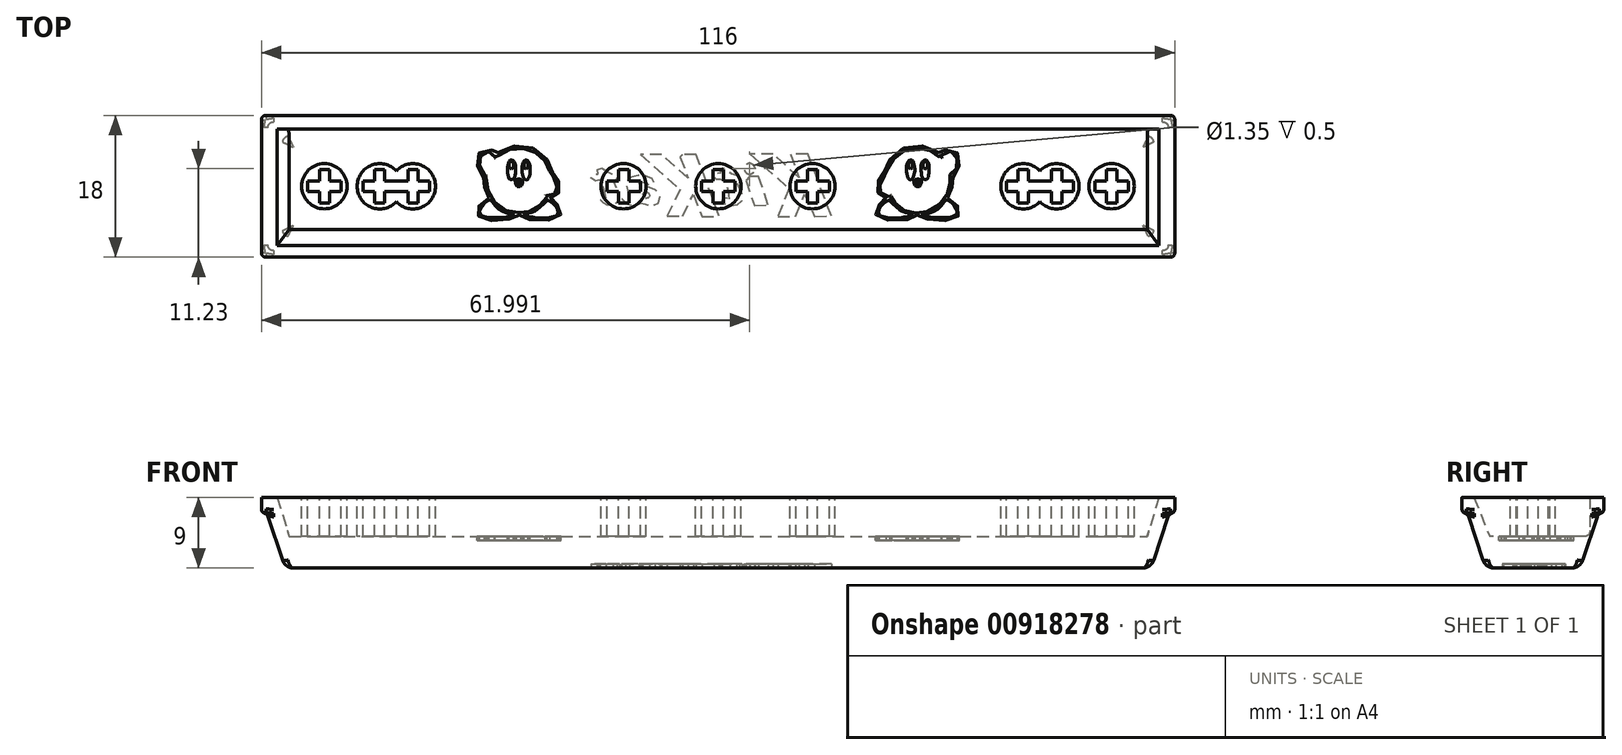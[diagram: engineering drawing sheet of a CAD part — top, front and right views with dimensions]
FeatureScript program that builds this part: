
annotation { "Feature Type Name" : "Feature", "Feature Type Description" : "" }
export const myFeature = defineFeature(function(context is Context, id is Id, definition is map)
    precondition{}
    {
        {
            var Q0;
            Q0=qCreatedBy(makeId("Top.planeOp"),FACE);
            var sketch = newSketch(context, id + "F0", { "sketchPlane" : qUnion([Q0])});
            skLineSegment(sketch, "E0", {"start": v(0, 0) * mm, "end": v(116, 0) * mm});
            skLineSegment(sketch, "E1", {"start": v(116, 0) * mm, "end": v(116, 18) * mm});
            skLineSegment(sketch, "E2", {"start": v(116, 18) * mm, "end": v(0, 18) * mm});
            skLineSegment(sketch, "E3", {"start": v(0, 18) * mm, "end": v(0, 0) * mm});
            skCircle(sketch, "E4", {"center": v(58.02, 9) * mm, "radius": 2.87 * mm});
            skLineSegment(sketch, "E5", {"start": v(60.13, 8.33) * mm, "end": v(58.65, 8.33) * mm});
            skLineSegment(sketch, "E6", {"start": v(55.88, 9.68) * mm, "end": v(57.35, 9.68) * mm});
            skLineSegment(sketch, "E7", {"start": v(57.35, 11.13) * mm, "end": v(57.35, 9.68) * mm});
            skLineSegment(sketch, "E8", {"start": v(58.65, 11.13) * mm, "end": v(58.65, 9.68) * mm});
            skLineSegment(sketch, "E9.trimOffspring", {"start": v(57.35, 8.33) * mm, "end": v(57.35, 6.88) * mm});
            skLineSegment(sketch, "E10.trimOffspring", {"start": v(58.65, 8.33) * mm, "end": v(58.65, 6.88) * mm});
            skLineSegment(sketch, "E11.trimOffspring", {"start": v(58.65, 9.68) * mm, "end": v(60.13, 9.68) * mm});
            skLineSegment(sketch, "E12.trimOffspring", {"start": v(57.35, 8.33) * mm, "end": v(55.88, 8.33) * mm});
            skLineSegment(sketch, "E13", {"start": v(55.88, 9.68) * mm, "end": v(55.88, 8.33) * mm});
            skLineSegment(sketch, "E14", {"start": v(57.35, 11.13) * mm, "end": v(58.65, 11.13) * mm});
            skLineSegment(sketch, "E15", {"start": v(60.13, 9.68) * mm, "end": v(60.13, 8.33) * mm});
            skLineSegment(sketch, "E16", {"start": v(57.35, 6.88) * mm, "end": v(58.65, 6.88) * mm});
            skLineSegment(sketch, "E17.MirrorCS", {"start": v(10.12, 9.68) * mm, "end": v(10.12, 8.33) * mm});
            skLineSegment(sketch, "E18.MirrorCS", {"start": v(7.35, 11.13) * mm, "end": v(7.35, 9.68) * mm});
            skLineSegment(sketch, "E19.MirrorCS", {"start": v(5.87, 9.68) * mm, "end": v(5.87, 8.33) * mm});
            skLineSegment(sketch, "E20.MirrorCS", {"start": v(7.35, 8.33) * mm, "end": v(7.35, 6.88) * mm});
            skLineSegment(sketch, "E21.MirrorCS", {"start": v(8.65, 8.33) * mm, "end": v(10.12, 8.33) * mm});
            skLineSegment(sketch, "E22.MirrorCS", {"start": v(8.65, 11.13) * mm, "end": v(8.65, 9.68) * mm});
            skLineSegment(sketch, "E23.MirrorCS", {"start": v(5.87, 8.33) * mm, "end": v(7.35, 8.33) * mm});
            skLineSegment(sketch, "E24.MirrorCS", {"start": v(8.65, 11.13) * mm, "end": v(7.35, 11.13) * mm});
            skLineSegment(sketch, "E25.MirrorCS", {"start": v(8.65, 6.88) * mm, "end": v(7.35, 6.88) * mm});
            skLineSegment(sketch, "E26.MirrorCS", {"start": v(10.12, 9.68) * mm, "end": v(8.65, 9.68) * mm});
            skLineSegment(sketch, "E27.MirrorCS", {"start": v(8.65, 8.33) * mm, "end": v(8.65, 6.88) * mm});
            skLineSegment(sketch, "E28.MirrorCS", {"start": v(7.35, 9.68) * mm, "end": v(5.87, 9.68) * mm});
            skCircle(sketch, "E29.MirrorC", {"center": v(7.98, 9) * mm, "radius": 2.87 * mm});
            skLineSegment(sketch, "E30.MirrorCS", {"start": v(108.65, 11.13) * mm, "end": v(108.65, 9.68) * mm});
            skLineSegment(sketch, "E31.MirrorCS", {"start": v(108.65, 8.33) * mm, "end": v(110.12, 8.33) * mm});
            skLineSegment(sketch, "E32.MirrorCS", {"start": v(110.12, 9.68) * mm, "end": v(110.12, 8.33) * mm});
            skLineSegment(sketch, "E33.MirrorCS", {"start": v(105.87, 8.33) * mm, "end": v(107.35, 8.33) * mm});
            skLineSegment(sketch, "E34.MirrorCS", {"start": v(110.12, 9.68) * mm, "end": v(108.65, 9.68) * mm});
            skLineSegment(sketch, "E35.MirrorCS", {"start": v(105.87, 9.68) * mm, "end": v(105.87, 8.33) * mm});
            skLineSegment(sketch, "E36.MirrorCS", {"start": v(108.65, 8.33) * mm, "end": v(108.65, 6.88) * mm});
            skLineSegment(sketch, "E37.MirrorCS", {"start": v(107.35, 11.13) * mm, "end": v(107.35, 9.68) * mm});
            skLineSegment(sketch, "E38.MirrorCS", {"start": v(108.65, 6.88) * mm, "end": v(107.35, 6.88) * mm});
            skLineSegment(sketch, "E39.MirrorCS", {"start": v(108.65, 11.13) * mm, "end": v(107.35, 11.13) * mm});
            skLineSegment(sketch, "E40.MirrorCS", {"start": v(107.35, 8.33) * mm, "end": v(107.35, 6.88) * mm});
            skLineSegment(sketch, "E41.MirrorCS", {"start": v(107.35, 9.68) * mm, "end": v(105.87, 9.68) * mm});
            skCircle(sketch, "E42.MirrorC", {"center": v(107.98, 9) * mm, "radius": 2.87 * mm});
            skLineSegment(sketch, "E43.MirrorCS", {"start": v(70.65, 8.33) * mm, "end": v(72.12, 8.33) * mm});
            skCircle(sketch, "E44.MirrorC", {"center": v(69.98, 9) * mm, "radius": 2.87 * mm});
            skLineSegment(sketch, "E45.MirrorCS", {"start": v(70.65, 6.88) * mm, "end": v(69.35, 6.88) * mm});
            skLineSegment(sketch, "E46.MirrorCS", {"start": v(67.87, 8.33) * mm, "end": v(69.35, 8.33) * mm});
            skLineSegment(sketch, "E47.MirrorCS", {"start": v(72.12, 9.68) * mm, "end": v(70.65, 9.68) * mm});
            skLineSegment(sketch, "E48.MirrorCS", {"start": v(67.87, 9.68) * mm, "end": v(67.87, 8.33) * mm});
            skLineSegment(sketch, "E49.MirrorCS", {"start": v(70.65, 11.13) * mm, "end": v(70.65, 9.68) * mm});
            skLineSegment(sketch, "E50.MirrorCS", {"start": v(72.12, 9.68) * mm, "end": v(72.12, 8.33) * mm});
            skLineSegment(sketch, "E51.MirrorCS", {"start": v(69.35, 9.68) * mm, "end": v(67.87, 9.68) * mm});
            skLineSegment(sketch, "E52.MirrorCS", {"start": v(69.35, 11.13) * mm, "end": v(69.35, 9.68) * mm});
            skLineSegment(sketch, "E53.MirrorCS", {"start": v(69.35, 8.33) * mm, "end": v(69.35, 6.88) * mm});
            skLineSegment(sketch, "E54.MirrorCS", {"start": v(70.65, 11.13) * mm, "end": v(69.35, 11.13) * mm});
            skLineSegment(sketch, "E55.MirrorCS", {"start": v(70.65, 8.33) * mm, "end": v(70.65, 6.88) * mm});
            skLineSegment(sketch, "E56.MirrorCS", {"start": v(43.87, 8.33) * mm, "end": v(45.35, 8.33) * mm});
            skLineSegment(sketch, "E57.MirrorCS", {"start": v(46.65, 11.13) * mm, "end": v(46.65, 9.68) * mm});
            skLineSegment(sketch, "E58.MirrorCS", {"start": v(45.35, 11.13) * mm, "end": v(45.35, 9.68) * mm});
            skLineSegment(sketch, "E59.MirrorCS", {"start": v(43.87, 9.68) * mm, "end": v(43.87, 8.33) * mm});
            skLineSegment(sketch, "E60.MirrorCS", {"start": v(45.35, 9.68) * mm, "end": v(43.87, 9.68) * mm});
            skLineSegment(sketch, "E61.MirrorCS", {"start": v(46.65, 8.33) * mm, "end": v(46.65, 6.88) * mm});
            skCircle(sketch, "E62.MirrorC", {"center": v(45.98, 9) * mm, "radius": 2.87 * mm});
            skLineSegment(sketch, "E63.MirrorCS", {"start": v(46.65, 8.33) * mm, "end": v(48.12, 8.33) * mm});
            skLineSegment(sketch, "E64.MirrorCS", {"start": v(45.35, 8.33) * mm, "end": v(45.35, 6.88) * mm});
            skLineSegment(sketch, "E65.MirrorCS", {"start": v(48.12, 9.68) * mm, "end": v(46.65, 9.68) * mm});
            skLineSegment(sketch, "E66.MirrorCS", {"start": v(46.65, 6.88) * mm, "end": v(45.35, 6.88) * mm});
            skLineSegment(sketch, "E67.MirrorCS", {"start": v(46.65, 11.13) * mm, "end": v(45.35, 11.13) * mm});
            skLineSegment(sketch, "E68.MirrorCS", {"start": v(48.12, 9.68) * mm, "end": v(48.12, 8.33) * mm});
            skLineSegment(sketch, "E69.MirrorCS", {"start": v(14.35, 11.13) * mm, "end": v(15.65, 11.13) * mm});
            skLineSegment(sketch, "E70.MirrorCS", {"start": v(15.65, 8.33) * mm, "end": v(15.65, 6.88) * mm});
            skLineSegment(sketch, "E71.MirrorCS", {"start": v(17.12, 8.33) * mm, "end": v(15.65, 8.33) * mm});
            skLineSegment(sketch, "E72.MirrorCS", {"start": v(12.87, 9.68) * mm, "end": v(14.35, 9.68) * mm});
            skLineSegment(sketch, "E73.MirrorCS", {"start": v(15.65, 9.68) * mm, "end": v(17.12, 9.68) * mm});
            skLineSegment(sketch, "E74.MirrorCS", {"start": v(14.35, 8.33) * mm, "end": v(12.87, 8.33) * mm});
            skLineSegment(sketch, "E75.MirrorCS", {"start": v(14.35, 6.88) * mm, "end": v(15.65, 6.88) * mm});
            skLineSegment(sketch, "E76.MirrorCS", {"start": v(15.65, 11.13) * mm, "end": v(15.65, 9.68) * mm});
            skLineSegment(sketch, "E77.MirrorCS", {"start": v(14.35, 8.33) * mm, "end": v(14.35, 6.88) * mm});
            skLineSegment(sketch, "E78.MirrorCS", {"start": v(12.87, 9.68) * mm, "end": v(12.87, 8.33) * mm});
            skLineSegment(sketch, "E79.MirrorCS", {"start": v(14.35, 11.13) * mm, "end": v(14.35, 9.68) * mm});
            skArc(sketch, "E80.MirrorC", {"start": v(17.12, 10.96) * mm, "mid": v(12.14, 9) * mm, "end": v(17.12, 7.05) * mm});
            skLineSegment(sketch, "E81.MirrorCS", {"start": v(19.9, 11.13) * mm, "end": v(18.6, 11.13) * mm});
            skLineSegment(sketch, "E82.MirrorCS", {"start": v(18.6, 11.13) * mm, "end": v(18.6, 9.68) * mm});
            skArc(sketch, "E83.MirrorC", {"start": v(17.12, 10.96) * mm, "mid": v(22.1, 9) * mm, "end": v(17.12, 7.05) * mm});
            skLineSegment(sketch, "E84.MirrorCS", {"start": v(18.6, 8.33) * mm, "end": v(18.6, 6.88) * mm});
            skLineSegment(sketch, "E85.MirrorCS", {"start": v(21.37, 9.68) * mm, "end": v(19.9, 9.68) * mm});
            skLineSegment(sketch, "E86.MirrorCS", {"start": v(21.37, 9.68) * mm, "end": v(21.37, 8.33) * mm});
            skLineSegment(sketch, "E87.MirrorCS", {"start": v(19.9, 8.33) * mm, "end": v(21.37, 8.33) * mm});
            skLineSegment(sketch, "E88.MirrorCS", {"start": v(19.9, 11.13) * mm, "end": v(19.9, 9.68) * mm});
            skLineSegment(sketch, "E89.MirrorCS", {"start": v(17.12, 8.33) * mm, "end": v(18.6, 8.33) * mm});
            skLineSegment(sketch, "E90.MirrorCS", {"start": v(19.9, 8.33) * mm, "end": v(19.9, 6.88) * mm});
            skLineSegment(sketch, "E91.MirrorCS", {"start": v(19.9, 6.88) * mm, "end": v(18.6, 6.88) * mm});
            skLineSegment(sketch, "E92.MirrorCS", {"start": v(18.6, 9.68) * mm, "end": v(17.12, 9.68) * mm});
            skLineSegment(sketch, "E93.MirrorCS", {"start": v(96.1, 6.88) * mm, "end": v(97.4, 6.88) * mm});
            skLineSegment(sketch, "E94.MirrorCS", {"start": v(96.1, 11.13) * mm, "end": v(97.4, 11.13) * mm});
            skLineSegment(sketch, "E95.MirrorCS", {"start": v(101.65, 6.88) * mm, "end": v(100.35, 6.88) * mm});
            skLineSegment(sketch, "E96.MirrorCS", {"start": v(101.65, 11.13) * mm, "end": v(100.35, 11.13) * mm});
            skLineSegment(sketch, "E97.MirrorCS", {"start": v(100.35, 8.33) * mm, "end": v(100.35, 6.88) * mm});
            skLineSegment(sketch, "E98.MirrorCS", {"start": v(98.88, 8.33) * mm, "end": v(100.35, 8.33) * mm});
            skLineSegment(sketch, "E99.MirrorCS", {"start": v(94.63, 9.68) * mm, "end": v(96.1, 9.68) * mm});
            skLineSegment(sketch, "E100.MirrorCS", {"start": v(103.13, 9.68) * mm, "end": v(101.65, 9.68) * mm});
            skLineSegment(sketch, "E101.MirrorCS", {"start": v(97.4, 9.68) * mm, "end": v(98.88, 9.68) * mm});
            skLineSegment(sketch, "E102.MirrorCS", {"start": v(96.1, 11.13) * mm, "end": v(96.1, 9.68) * mm});
            skArc(sketch, "E103.MirrorCS", {"start": v(98.88, 10.96) * mm, "mid": v(103.86, 9) * mm, "end": v(98.88, 7.05) * mm});
            skLineSegment(sketch, "E104.MirrorCS", {"start": v(97.4, 11.13) * mm, "end": v(97.4, 9.68) * mm});
            skLineSegment(sketch, "E105.MirrorCS", {"start": v(97.4, 8.33) * mm, "end": v(97.4, 6.88) * mm});
            skLineSegment(sketch, "E106.MirrorCS", {"start": v(103.13, 9.68) * mm, "end": v(103.13, 8.33) * mm});
            skLineSegment(sketch, "E107.MirrorCS", {"start": v(100.35, 11.13) * mm, "end": v(100.35, 9.68) * mm});
            skLineSegment(sketch, "E108.MirrorCS", {"start": v(101.65, 8.33) * mm, "end": v(101.65, 6.88) * mm});
            skLineSegment(sketch, "E109.MirrorCS", {"start": v(96.1, 8.33) * mm, "end": v(94.63, 8.33) * mm});
            skLineSegment(sketch, "E110.MirrorCS", {"start": v(100.35, 9.68) * mm, "end": v(98.88, 9.68) * mm});
            skArc(sketch, "E111.MirrorCS", {"start": v(98.88, 10.96) * mm, "mid": v(93.9, 9) * mm, "end": v(98.88, 7.05) * mm});
            skLineSegment(sketch, "E112.MirrorCS", {"start": v(98.88, 8.33) * mm, "end": v(97.4, 8.33) * mm});
            skLineSegment(sketch, "E113.MirrorCS", {"start": v(94.63, 9.68) * mm, "end": v(94.63, 8.33) * mm});
            skLineSegment(sketch, "E114.MirrorCS", {"start": v(101.65, 11.13) * mm, "end": v(101.65, 9.68) * mm});
            skLineSegment(sketch, "E115.MirrorCS", {"start": v(96.1, 8.33) * mm, "end": v(96.1, 6.88) * mm});
            skLineSegment(sketch, "E116.MirrorCS", {"start": v(101.65, 8.33) * mm, "end": v(103.13, 8.33) * mm});
            skLineSegment(sketch, "E117", {"start": v(2, 2) * mm, "end": v(2, 15.75) * mm});
            skLineSegment(sketch, "E118", {"start": v(2, 15.75) * mm, "end": v(114, 15.75) * mm});
            skLineSegment(sketch, "E119", {"start": v(114, 15.75) * mm, "end": v(114, 2) * mm});
            skLineSegment(sketch, "E120", {"start": v(114, 2) * mm, "end": v(2, 2) * mm});
            skPoint(sketch, "E121.orphan", {"position": v(114, 0) * mm});
            skLineSegment(sketch, "E122", {"start": v(3.5, 4) * mm, "end": v(3.5, 15.75) * mm});
            skLineSegment(sketch, "E123", {"start": v(3.5, 4) * mm, "end": v(112.5, 4) * mm});
            skLineSegment(sketch, "E124", {"start": v(112.5, 15.75) * mm, "end": v(112.5, 4) * mm});
            skPoint(sketch, "E125.orphan", {"position": v(3.5, 2) * mm});
            skLineSegment(sketch, "E126.trimOffspring", {"start": v(58, 2) * mm, "end": v(58, 0) * mm});
            skSolve(sketch);
        }
        {
            var Q0;
            Q0=qCreatedBy(makeId("Top.planeOp"),FACE);
            var sketch = newSketch(context, id + "F1", { "sketchPlane" : qUnion([Q0])});
            skLineSegment(sketch, "E127.0", {"start": v(2, 16.25) * mm, "end": v(114, 16.25) * mm});
            skLineSegment(sketch, "E127.1", {"start": v(2, 1.5) * mm, "end": v(2, 16.25) * mm});
            skLineSegment(sketch, "E127.2", {"start": v(114, 1.5) * mm, "end": v(2, 1.5) * mm});
            skLineSegment(sketch, "E127.3", {"start": v(114, 16.25) * mm, "end": v(114, 1.5) * mm});
            skSolve(sketch);
        }
        {
            var Q0;
            Q0=qCreatedBy(makeId("Top.planeOp"),FACE);
            cPlane(context, id + "F2", {"entities" : qUnion([Q0]), "cplaneType" : CPlaneType.OFFSET, "offset" : 5 * mm, "oppositeDirection" : true, "width" : 150 * mm, "height" : 150 * mm});
        }
        {
            var Q0;
            Q0=qCreatedBy(id+"F2.planeOp",FACE);
            var sketch = newSketch(context, id + "F3", { "sketchPlane" : qUnion([Q0])});
            skLineSegment(sketch, "E128.0", {"start": v(3.5, 16.25) * mm, "end": v(112.5, 16.25) * mm});
            skLineSegment(sketch, "E128.1", {"start": v(3.5, 3.5) * mm, "end": v(3.5, 16.25) * mm});
            skLineSegment(sketch, "E128.2", {"start": v(3.5, 3.5) * mm, "end": v(112.5, 3.5) * mm});
            skLineSegment(sketch, "E128.3", {"start": v(112.5, 16.25) * mm, "end": v(112.5, 3.5) * mm});
            skPoint(sketch, "E129.orphan", {"position": v(2, 15.75) * mm});
            skPoint(sketch, "E130.orphan", {"position": v(114, 15.75) * mm});
            skSolve(sketch);
        }
        {
            var Q0;
            Q0=qCreatedBy(makeId("Top.planeOp"),FACE);
            var sketch = newSketch(context, id + "F4", { "sketchPlane" : qUnion([Q0])});
            skLineSegment(sketch, "E131.0", {"start": v(116, 18) * mm, "end": v(0, 18) * mm});
            skLineSegment(sketch, "E131.1", {"start": v(0, 18) * mm, "end": v(0, 0) * mm});
            skLineSegment(sketch, "E131.2", {"start": v(0, 0) * mm, "end": v(116, 0) * mm});
            skLineSegment(sketch, "E131.3", {"start": v(116, 0) * mm, "end": v(116, 18) * mm});
            skSolve(sketch);
        }
        {
            var Q0;
            Q0=qCreatedBy(makeId("Top.planeOp"),FACE);
            cPlane(context, id + "F5", {"entities" : qUnion([Q0]), "cplaneType" : CPlaneType.OFFSET, "offset" : 9 * mm, "oppositeDirection" : true, "width" : 150 * mm, "height" : 150 * mm});
        }
        {
            var Q0;
            Q0=qCreatedBy(id+"F5.planeOp",FACE);
            var sketch = newSketch(context, id + "F6", { "sketchPlane" : qUnion([Q0])});
            skLineSegment(sketch, "E132", {"start": v(3, 3) * mm, "end": v(113, 3) * mm});
            skLineSegment(sketch, "E133", {"start": v(113, 3) * mm, "end": v(113, 15) * mm});
            skLineSegment(sketch, "E134", {"start": v(113, 15) * mm, "end": v(3, 15) * mm});
            skLineSegment(sketch, "E135", {"start": v(3, 15) * mm, "end": v(3, 3) * mm});
            skSolve(sketch);
        }
        {
            var Q0;
            Q0=makeQuery(id+"F4.imprint","IMPRINT",FACE,{"disambiguationData":[TD([[makeQuery(id+"F4.imprint","IMPRINT",EDGE,{"derivedFrom":sQuery(id+"F4.wireOp",EDGE,"E131.0")}),1.0]])]});
            var Q1;
            Q1=makeQuery(id+"F6.imprint","IMPRINT",FACE,{"disambiguationData":[TD([[makeQuery(id+"F6.imprint","IMPRINT",EDGE,{"derivedFrom":sQuery(id+"F6.wireOp",EDGE,"E132")}),1.0]])]});
            loft(context, id + "F7", {"sheetProfilesArray" : [{ "sheetProfileEntities" : qUnion([Q0]) }, { "sheetProfileEntities" : qUnion([Q1]) }]});
        }
        {
            var Q1;
            Q1=makeQuery(id+"F1.imprint","IMPRINT",FACE,{"disambiguationData":[TD([[makeQuery(id+"F1.imprint","IMPRINT",EDGE,{"derivedFrom":sQuery(id+"F1.wireOp",EDGE,"E127.0")}),-1.0]])]});
            var Q2;
            Q2=makeQuery(id+"F3.imprint","IMPRINT",FACE,{"disambiguationData":[TD([[makeQuery(id+"F3.imprint","IMPRINT",EDGE,{"derivedFrom":sQuery(id+"F3.wireOp",EDGE,"E128.0")}),-1.0]])]});
            loft(context, id + "F8", {"operationType" : NewBodyOperationType.REMOVE, "sheetProfilesArray" : [{ "sheetProfileEntities" : qUnion([Q1]) }, { "sheetProfileEntities" : qUnion([Q2]) }]});
        }
        {
            var Q0;
            Q0=makeQuery(id+"F0.imprint","IMPRINT",FACE,{"disambiguationData":[TD([[makeQuery(id+"F0.imprint","IMPRINT",EDGE,{"derivedFrom":sQuery(id+"F0.wireOp",EDGE,"E17.MirrorCS")}),1.0]])]});
            var Q1;
            Q1=makeQuery(id+"F0.imprint","IMPRINT",FACE,{"disambiguationData":[TD([[makeQuery(id+"F0.imprint","IMPRINT",EDGE,{"derivedFrom":sQuery(id+"F0.wireOp",EDGE,"E69.MirrorCS")}),1.0]])]});
            var Q2;
            Q2=makeQuery(id+"F0.imprint","IMPRINT",FACE,{"disambiguationData":[TD([[makeQuery(id+"F0.imprint","IMPRINT",EDGE,{"derivedFrom":sQuery(id+"F0.wireOp",EDGE,"E56.MirrorCS")}),-1.0]])]});
            var Q3;
            Q3=makeQuery(id+"F0.imprint","IMPRINT",FACE,{"disambiguationData":[TD([[makeQuery(id+"F0.imprint","IMPRINT",EDGE,{"derivedFrom":sQuery(id+"F0.wireOp",EDGE,"E4")}),1.0]])]});
            var Q4;
            Q4=makeQuery(id+"F0.imprint","IMPRINT",FACE,{"disambiguationData":[TD([[makeQuery(id+"F0.imprint","IMPRINT",EDGE,{"derivedFrom":sQuery(id+"F0.wireOp",EDGE,"E43.MirrorCS")}),-1.0]])]});
            var Q5;
            Q5=makeQuery(id+"F0.imprint","IMPRINT",FACE,{"disambiguationData":[TD([[makeQuery(id+"F0.imprint","IMPRINT",EDGE,{"derivedFrom":sQuery(id+"F0.wireOp",EDGE,"E93.MirrorCS")}),-1.0]])]});
            var Q6;
            Q6=makeQuery(id+"F0.imprint","IMPRINT",FACE,{"disambiguationData":[TD([[makeQuery(id+"F0.imprint","IMPRINT",EDGE,{"derivedFrom":sQuery(id+"F0.wireOp",EDGE,"E30.MirrorCS")}),1.0]])]});
            extrude(context, id + "F9", {"entities" : qUnion([Q0, Q1, Q2, Q3, Q4, Q5, Q6]), "operationType" : NewBodyOperationType.ADD, "endBound" : BoundingType.UP_TO_NEXT, "oppositeDirection" : true, "depth" : 25 * mm, "offsetDistance" : 25 * mm});
        }
        {
            var Q0;
            Q0=makeQuery(id+"F7.opLoft","CAP_FACE",FACE,{"disambiguationData":[OSD([makeQuery(id+"F4.imprint","IMPRINT",FACE,{"disambiguationData":[TD([[makeQuery(id+"F4.imprint","IMPRINT",EDGE,{"derivedFrom":sQuery(id+"F4.wireOp",EDGE,"E131.0")}),1.0]])]})])],"isStart":true});
            extrude(context, id + "F10", {"entities" : qUnion([Q0]), "operationType" : NewBodyOperationType.ADD, "oppositeDirection" : true, "depth" : 2 * mm, "offsetDistance" : 25 * mm});
        }
        {
            var Q0;
            Q0=makeQuery(id+"F7.opLoft","CAP_FACE",FACE,{"disambiguationData":[OSD([makeQuery(id+"F6.imprint","IMPRINT",FACE,{"disambiguationData":[TD([[makeQuery(id+"F6.imprint","IMPRINT",EDGE,{"derivedFrom":sQuery(id+"F6.wireOp",EDGE,"E132")}),1.0]])]})])],"isStart":true});
            var sketch = newSketch(context, id + "F11", { "sketchPlane" : qUnion([Q0])});
            skLineSegment(sketch, "E136", {"start": v(72.37, -5.24) * mm, "end": v(69.4, -13.12) * mm});
            skLineSegment(sketch, "E137", {"start": v(69.4, -13.12) * mm, "end": v(67.22, -13.12) * mm});
            skLineSegment(sketch, "E138", {"start": v(67.22, -13.12) * mm, "end": v(68.24, -10.12) * mm});
            skLineSegment(sketch, "E139", {"start": v(68.24, -10.12) * mm, "end": v(65, -13.09) * mm});
            skLineSegment(sketch, "E140", {"start": v(65, -13.09) * mm, "end": v(62.06, -13.09) * mm});
            skLineSegment(sketch, "E141", {"start": v(62.06, -13.09) * mm, "end": v(67.01, -8.72) * mm});
            skLineSegment(sketch, "E142", {"start": v(67.01, -8.72) * mm, "end": v(65.58, -5.17) * mm});
            skLineSegment(sketch, "E143", {"start": v(65.58, -5.17) * mm, "end": v(67.83, -5.17) * mm});
            skLineSegment(sketch, "E144", {"start": v(67.83, -5.17) * mm, "end": v(68.99, -8.04) * mm});
            skLineSegment(sketch, "E145", {"start": v(68.99, -8.04) * mm, "end": v(70.25, -5.17) * mm});
            skLineSegment(sketch, "E146", {"start": v(70.25, -5.17) * mm, "end": v(72.37, -5.24) * mm});
            skLineSegment(sketch, "E147", {"start": v(64.35, -6.64) * mm, "end": v(63.12, -10.23) * mm});
            skLineSegment(sketch, "E148", {"start": v(63.12, -10.23) * mm, "end": v(61.96, -10.23) * mm});
            skLineSegment(sketch, "E149", {"start": v(61.96, -10.23) * mm, "end": v(61.51, -9.75) * mm});
            skLineSegment(sketch, "E150", {"start": v(61.51, -9.75) * mm, "end": v(62.61, -6.53) * mm});
            skLineSegment(sketch, "E151", {"start": v(62.61, -6.53) * mm, "end": v(64.35, -6.64) * mm});
            skLineSegment(sketch, "E152", {"start": v(58.14, -5.2) * mm, "end": v(55.2, -13.02) * mm});
            skLineSegment(sketch, "E153", {"start": v(55.2, -13.02) * mm, "end": v(53.47, -13.02) * mm});
            skLineSegment(sketch, "E154", {"start": v(53.47, -13.02) * mm, "end": v(53.17, -12.7) * mm});
            skLineSegment(sketch, "E155", {"start": v(53.17, -12.7) * mm, "end": v(54.15, -10.08) * mm});
            skLineSegment(sketch, "E156", {"start": v(54.15, -10.08) * mm, "end": v(50.82, -13.02) * mm});
            skLineSegment(sketch, "E157", {"start": v(50.82, -13.02) * mm, "end": v(48.14, -13.02) * mm});
            skLineSegment(sketch, "E158", {"start": v(48.14, -13.02) * mm, "end": v(53.17, -8.58) * mm});
            skLineSegment(sketch, "E159", {"start": v(53.17, -8.58) * mm, "end": v(51.52, -5.24) * mm});
            skLineSegment(sketch, "E160", {"start": v(51.52, -5.24) * mm, "end": v(53.47, -5.24) * mm});
            skLineSegment(sketch, "E161", {"start": v(53.47, -5.24) * mm, "end": v(54.86, -7.97) * mm});
            skLineSegment(sketch, "E162", {"start": v(54.86, -7.97) * mm, "end": v(55.93, -5.13) * mm});
            skLineSegment(sketch, "E163", {"start": v(55.93, -5.13) * mm, "end": v(58.14, -5.2) * mm});
            skFitSpline(sketch, "E164", {"points": [v(47.8, -10.4) * mm, v(46.47, -9.85) * mm, v(46.33, -8.96) * mm, v(46.7, -7.8) * mm, v(46.2, -7.8) * mm, v(45.75, -7.56) * mm, v(46.3, -6.84) * mm, v(47.46, -6.5) * mm, v(48.45, -6.91) * mm, v(48.82, -6.64) * mm, v(50.19, -6.67) * mm, v(50.63, -7.56) * mm, v(49.92, -8.65) * mm, v(48.86, -8.9) * mm, v(48.07, -9.1) * mm, v(48, -9.47) * mm, v(48.65, -9.47) * mm, v(49.44, -9.16) * mm, v(49.95, -9.64) * mm, v(48.86, -10.32) * mm, v(47.8, -10.4) * mm]});
            skFitSpline(sketch, "E165", {"points": [v(48.72, -8.28) * mm, v(49.27, -7.94) * mm, v(49.13, -7.56) * mm, v(48.42, -7.56) * mm, v(48.72, -8.28) * mm]});
            skPoint(sketch, "E166.1.internal.snap0", {"position": v(62.54, -10.23) * mm});
            skFitSpline(sketch, "E166", {"points": [v(43.26, -11.31) * mm, v(44.1, -10.7) * mm, v(45.07, -10.23) * mm, v(45.1, -9.75) * mm, v(44.7, -9.75) * mm, v(45.04, -8.9) * mm, v(45.45, -7.53) * mm, v(45.07, -6.8) * mm, v(43.88, -6.6) * mm, v(43.3, -7.01) * mm, v(43.02, -7.32) * mm, v(43.3, -7.53) * mm, v(43.74, -7.42) * mm, v(43.67, -8.07) * mm, v(43.02, -9.75) * mm, v(42.79, -9.75) * mm, v(42.03, -9.75) * mm, v(42, -10.56) * mm, v(42.72, -10.53) * mm, v(42.65, -11.04) * mm, v(43.26, -11.31) * mm]});
            skCircle(sketch, "E167", {"center": v(62, -11.23) * mm, "radius": 0.68 * mm});
            skPoint(sketch, "E168.15.internal.snap0", {"position": v(68.4, -6.6) * mm});
            skPoint(sketch, "E168.16.internal.snap0", {"position": v(68.4, -6.6) * mm});
            skFitSpline(sketch, "E168", {"points": [v(59.43, -7.4) * mm, v(58.72, -9.83) * mm, v(58.2, -9.8) * mm, v(57.59, -10) * mm, v(57.59, -10.62) * mm, v(58.17, -10.65) * mm, v(58.4, -10.79) * mm, v(58.24, -11.16) * mm, v(58.78, -11.33) * mm, v(59.3, -10.82) * mm, v(60.35, -10.38) * mm, v(60.7, -9.97) * mm, v(60.32, -9.52) * mm, v(60.42, -9.29) * mm, v(61.04, -7.48) * mm, v(60.32, -6.6) * mm, v(59.12, -6.6) * mm, v(58.51, -7.2) * mm, v(58.82, -7.58) * mm, v(59.43, -7.4) * mm]});
            skSolve(sketch);
        }
        {
            var Q0;
            Q0=makeQuery(id+"F11.imprint","IMPRINT",FACE,{"disambiguationData":[TD([[makeQuery(id+"F11.imprint","IMPRINT",EDGE,{"derivedFrom":sQuery(id+"F11.wireOp",EDGE,"E136")}),-1.0]])]});
            var Q1;
            Q1=makeQuery(id+"F11.imprint","IMPRINT",FACE,{"disambiguationData":[TD([[makeQuery(id+"F11.imprint","IMPRINT",EDGE,{"derivedFrom":sQuery(id+"F11.wireOp",EDGE,"E147")}),-1.0]])]});
            var Q2;
            Q2=makeQuery(id+"F11.imprint","IMPRINT",FACE,{"disambiguationData":[TD([[makeQuery(id+"F11.imprint","IMPRINT",EDGE,{"derivedFrom":sQuery(id+"F11.wireOp",EDGE,"E168")}),1.0]])]});
            var Q3;
            Q3=makeQuery(id+"F11.imprint","IMPRINT",FACE,{"disambiguationData":[TD([[makeQuery(id+"F11.imprint","IMPRINT",EDGE,{"derivedFrom":sQuery(id+"F11.wireOp",EDGE,"E152")}),-1.0]])]});
            var Q4;
            Q4=makeQuery(id+"F11.imprint","IMPRINT",FACE,{"disambiguationData":[TD([[makeQuery(id+"F11.imprint","IMPRINT",EDGE,{"derivedFrom":sQuery(id+"F11.wireOp",EDGE,"E164")}),-1.0]])]});
            var Q5;
            Q5=makeQuery(id+"F11.imprint","IMPRINT",FACE,{"disambiguationData":[TD([[makeQuery(id+"F11.imprint","IMPRINT",EDGE,{"derivedFrom":sQuery(id+"F11.wireOp",EDGE,"E166")}),1.0]])]});
            var Q6;
            Q6=makeQuery(id+"F11.imprint","IMPRINT",FACE,{"disambiguationData":[TD([[makeQuery(id+"F11.imprint","IMPRINT",EDGE,{"derivedFrom":sQuery(id+"F11.wireOp",EDGE,"E167")}),1.0]])]});
            extrude(context, id + "F12", {"entities" : qUnion([Q0, Q1, Q2, Q3, Q4, Q5, Q6]), "operationType" : NewBodyOperationType.REMOVE, "oppositeDirection" : true, "depth" : .5 * mm, "offsetDistance" : 25 * mm});
        }
        {
            var Q0;
            Q0=makeQuery(id+"F7.opLoft","MID_CAP_EDGE",EDGE,{"disambiguationData":[OSD([sQuery(id+"F6.wireOp",EDGE,"E132"),sQuery(id+"F6.wireOp",EDGE,"E133"),sQuery(id+"F6.wireOp",EDGE,"E135")])],"capPos":1.0});
            var Q1;
            Q1=makeQuery(id+"F7.opLoft","MID_CAP_EDGE",EDGE,{"disambiguationData":[OSD([sQuery(id+"F6.wireOp",EDGE,"E133"),sQuery(id+"F6.wireOp",EDGE,"E134"),sQuery(id+"F6.wireOp",EDGE,"E135")])],"capPos":1.0});
            var Q2;
            Q2=makeQuery(id+"F7.opLoft","MID_CAP_EDGE",EDGE,{"disambiguationData":[OSD([sQuery(id+"F6.wireOp",EDGE,"E132"),sQuery(id+"F6.wireOp",EDGE,"E134"),sQuery(id+"F6.wireOp",EDGE,"E135")])],"capPos":1.0});
            var Q3;
            Q3=makeQuery(id+"F7.opLoft","MID_CAP_EDGE",EDGE,{"disambiguationData":[OSD([sQuery(id+"F6.wireOp",EDGE,"E132"),sQuery(id+"F6.wireOp",EDGE,"E133"),sQuery(id+"F6.wireOp",EDGE,"E134")])],"capPos":1.0});
            fillet(context, id + "F13", {"entities" : qUnion([Q0, Q1, Q2, Q3]), "radius" : 1.5 * mm, "tangentPropagation" : true, "allowEdgeOverflow" : false});
        }
        {
            var Q0;
            Q0=makeQuery(id+"F7.opLoft","SWEPT_EDGE",EDGE,{"disambiguationData":[OSD([sQuery(id+"F4.wireOp",EDGE,"E131.1"),sQuery(id+"F4.wireOp",EDGE,"E131.2"),sQuery(id+"F6.wireOp",EDGE,"E132"),sQuery(id+"F6.wireOp",EDGE,"E135")])]});
            var Q1;
            Q1=makeQuery(id+"F7.opLoft","SWEPT_EDGE",EDGE,{"disambiguationData":[OSD([sQuery(id+"F4.wireOp",EDGE,"E131.0"),sQuery(id+"F4.wireOp",EDGE,"E131.1"),sQuery(id+"F6.wireOp",EDGE,"E134"),sQuery(id+"F6.wireOp",EDGE,"E135")])]});
            var Q2;
            Q2=makeQuery(id+"F7.opLoft","SWEPT_EDGE",EDGE,{"disambiguationData":[OSD([sQuery(id+"F4.wireOp",EDGE,"E131.0"),sQuery(id+"F4.wireOp",EDGE,"E131.3"),sQuery(id+"F6.wireOp",EDGE,"E133"),sQuery(id+"F6.wireOp",EDGE,"E134")])]});
            var Q3;
            Q3=makeQuery(id+"F7.opLoft","SWEPT_EDGE",EDGE,{"disambiguationData":[OSD([sQuery(id+"F4.wireOp",EDGE,"E131.2"),sQuery(id+"F4.wireOp",EDGE,"E131.3"),sQuery(id+"F6.wireOp",EDGE,"E132"),sQuery(id+"F6.wireOp",EDGE,"E133")])]});
            var Q4;
            {var subQ0=sQuery(id+"F4.wireOp",EDGE,"E131.1");var subQ1=sQuery(id+"F4.wireOp",EDGE,"E131.2");var subQ2=sQuery(id+"F4.wireOp",EDGE,"E131.3");Q4=makeQuery(id+"F10.boolean.opBoolean","INTERSECT",EDGE,{"derivedFrom":[makeQuery(id+"F7.opLoft","SWEPT_FACE",FACE,{"disambiguationData":[OSD([subQ0,subQ1,subQ2,sQuery(id+"F6.wireOp",EDGE,"E132"),sQuery(id+"F6.wireOp",EDGE,"E133"),sQuery(id+"F6.wireOp",EDGE,"E135")])]}),makeQuery(id+"F10.opExtrude","CAP_FACE",FACE,{"disambiguationData":[OSD([makeQuery(id+"F4.imprint","IMPRINT",FACE,{"disambiguationData":[TD([[makeQuery(id+"F4.imprint","IMPRINT",EDGE,{"derivedFrom":sQuery(id+"F4.wireOp",EDGE,"E131.0")}),1.0]])]})])],"isStart":false})]});}
            var Q5;
            {var subQ0=sQuery(id+"F4.wireOp",EDGE,"E131.0");var subQ1=sQuery(id+"F4.wireOp",EDGE,"E131.1");var subQ2=sQuery(id+"F4.wireOp",EDGE,"E131.2");Q5=makeQuery(id+"F10.boolean.opBoolean","INTERSECT",EDGE,{"derivedFrom":[makeQuery(id+"F7.opLoft","SWEPT_FACE",FACE,{"disambiguationData":[OSD([subQ0,subQ1,subQ2,sQuery(id+"F6.wireOp",EDGE,"E132"),sQuery(id+"F6.wireOp",EDGE,"E134"),sQuery(id+"F6.wireOp",EDGE,"E135")])]}),makeQuery(id+"F10.opExtrude","CAP_FACE",FACE,{"disambiguationData":[OSD([makeQuery(id+"F4.imprint","IMPRINT",FACE,{"disambiguationData":[TD([[makeQuery(id+"F4.imprint","IMPRINT",EDGE,{"derivedFrom":subQ0}),1.0]])]})])],"isStart":false})]});}
            var Q6;
            {var subQ0=sQuery(id+"F4.wireOp",EDGE,"E131.0");var subQ1=sQuery(id+"F4.wireOp",EDGE,"E131.1");var subQ2=sQuery(id+"F4.wireOp",EDGE,"E131.3");Q6=makeQuery(id+"F10.boolean.opBoolean","INTERSECT",EDGE,{"derivedFrom":[makeQuery(id+"F7.opLoft","SWEPT_FACE",FACE,{"disambiguationData":[OSD([subQ0,subQ1,subQ2,sQuery(id+"F6.wireOp",EDGE,"E133"),sQuery(id+"F6.wireOp",EDGE,"E134"),sQuery(id+"F6.wireOp",EDGE,"E135")])]}),makeQuery(id+"F10.opExtrude","CAP_FACE",FACE,{"disambiguationData":[OSD([makeQuery(id+"F4.imprint","IMPRINT",FACE,{"disambiguationData":[TD([[makeQuery(id+"F4.imprint","IMPRINT",EDGE,{"derivedFrom":subQ0}),1.0]])]})])],"isStart":false})]});}
            var Q7;
            {var subQ0=sQuery(id+"F4.wireOp",EDGE,"E131.0");var subQ1=sQuery(id+"F4.wireOp",EDGE,"E131.2");var subQ2=sQuery(id+"F4.wireOp",EDGE,"E131.3");Q7=makeQuery(id+"F10.boolean.opBoolean","INTERSECT",EDGE,{"derivedFrom":[makeQuery(id+"F7.opLoft","SWEPT_FACE",FACE,{"disambiguationData":[OSD([subQ0,subQ1,subQ2,sQuery(id+"F6.wireOp",EDGE,"E132"),sQuery(id+"F6.wireOp",EDGE,"E133"),sQuery(id+"F6.wireOp",EDGE,"E134")])]}),makeQuery(id+"F10.opExtrude","CAP_FACE",FACE,{"disambiguationData":[OSD([makeQuery(id+"F4.imprint","IMPRINT",FACE,{"disambiguationData":[TD([[makeQuery(id+"F4.imprint","IMPRINT",EDGE,{"derivedFrom":subQ0}),1.0]])]})])],"isStart":false})]});}
            fillet(context, id + "F14", {"entities" : qUnion([Q0, Q1, Q2, Q3, Q4, Q5, Q6, Q7]), "radius" : .75 * mm, "tangentPropagation" : true, "allowEdgeOverflow" : false});
        }
        {
            var Q0;
            Q0=makeQuery(id+"F10.opExtrude","CAP_EDGE",EDGE,{"disambiguationData":[OSD([sQuery(id+"F4.wireOp",EDGE,"E131.0"),sQuery(id+"F4.wireOp",EDGE,"E131.1"),sQuery(id+"F4.wireOp",EDGE,"E131.2")])],"isStart":false});
            var Q1;
            Q1=makeQuery(id+"F10.opExtrude","CAP_EDGE",EDGE,{"disambiguationData":[OSD([sQuery(id+"F4.wireOp",EDGE,"E131.0"),sQuery(id+"F4.wireOp",EDGE,"E131.1"),sQuery(id+"F4.wireOp",EDGE,"E131.3")])],"isStart":false});
            var Q2;
            Q2=makeQuery(id+"F10.opExtrude","CAP_EDGE",EDGE,{"disambiguationData":[OSD([sQuery(id+"F4.wireOp",EDGE,"E131.1"),sQuery(id+"F4.wireOp",EDGE,"E131.2"),sQuery(id+"F4.wireOp",EDGE,"E131.3")])],"isStart":false});
            var Q3;
            Q3=makeQuery(id+"F10.opExtrude","CAP_EDGE",EDGE,{"disambiguationData":[OSD([sQuery(id+"F4.wireOp",EDGE,"E131.0"),sQuery(id+"F4.wireOp",EDGE,"E131.2"),sQuery(id+"F4.wireOp",EDGE,"E131.3")])],"isStart":false});
            var Q4;
            Q4=makeQuery(id+"F10.opExtrude","SWEPT_EDGE",EDGE,{"disambiguationData":[OSD([sQuery(id+"F4.wireOp",EDGE,"E131.2"),sQuery(id+"F4.wireOp",EDGE,"E131.3")])]});
            var Q5;
            Q5=makeQuery(id+"F10.opExtrude","SWEPT_EDGE",EDGE,{"disambiguationData":[OSD([sQuery(id+"F4.wireOp",EDGE,"E131.0"),sQuery(id+"F4.wireOp",EDGE,"E131.3")])]});
            var Q6;
            Q6=makeQuery(id+"F10.opExtrude","SWEPT_EDGE",EDGE,{"disambiguationData":[OSD([sQuery(id+"F4.wireOp",EDGE,"E131.0"),sQuery(id+"F4.wireOp",EDGE,"E131.1")])]});
            var Q7;
            Q7=makeQuery(id+"F10.opExtrude","SWEPT_EDGE",EDGE,{"disambiguationData":[OSD([sQuery(id+"F4.wireOp",EDGE,"E131.1"),sQuery(id+"F4.wireOp",EDGE,"E131.2")])]});
            fillet(context, id + "F15", {"entities" : qUnion([Q0, Q1, Q2, Q3, Q4, Q5, Q6, Q7]), "radius" : .5 * mm, "tangentPropagation" : true, "allowEdgeOverflow" : false});
        }
        {
            var Q0;
            Q0=makeQuery(id+"F8.boolean.opBoolean","COPY",EDGE,{"derivedFrom":makeQuery(id+"F8.opLoft","MID_CAP_EDGE",EDGE,{"disambiguationData":[OSD([sQuery(id+"F3.wireOp",EDGE,"E128.0"),sQuery(id+"F3.wireOp",EDGE,"E128.1"),sQuery(id+"F3.wireOp",EDGE,"E128.3")])],"capPos":1.0})});
            fillet(context, id + "F16", {"entities" : qUnion([Q0]), "radius" : .75 * mm, "tangentPropagation" : true, "allowEdgeOverflow" : false});
        }
        {
            var Q0;
            {var subQ2=sQuery(id+"F3.wireOp",EDGE,"E128.0");Q0=makeQuery(id+"F9.boolean.opBoolean","SPLIT",FACE,{"disambiguationData":[TD([makeQuery(id+"F9.opExtrude","SWEPT_FACE",FACE,{"disambiguationData":[OSD([sQuery(id+"F0.wireOp",EDGE,"E4")])]})])],"derivedFrom":makeQuery(id+"F8.boolean.opBoolean","COPY",FACE,{"derivedFrom":makeQuery(id+"F8.opLoft","CAP_FACE",FACE,{"disambiguationData":[OSD([makeQuery(id+"F3.imprint","IMPRINT",FACE,{"disambiguationData":[TD([[makeQuery(id+"F3.imprint","IMPRINT",EDGE,{"derivedFrom":subQ2}),-1.0]])]})])],"isStart":true})})});}
            var sketch = newSketch(context, id + "F17", { "sketchPlane" : qUnion([Q0])});
            skFitSpline(sketch, "E169", {"points": [v(28.92, 7.48) * mm, v(28.55, 8.18) * mm, v(28.3, 9.22) * mm, v(28.37, 9.98) * mm, v(28.1, 10.2) * mm, v(27.55, 11.17) * mm, v(27.36, 12.36) * mm, v(27.73, 13.33) * mm, v(28.77, 13.73) * mm, v(29.68, 13.27) * mm, v(29.86, 13.12) * mm, v(30.02, 13.27) * mm, v(31.63, 14.03) * mm, v(33.98, 14) * mm, v(35.63, 13.09) * mm, v(36.78, 11.41) * mm, v(36.97, 10.68) * mm, v(37.27, 10.44) * mm, v(37.73, 9.61) * mm, v(37.82, 8.64) * mm, v(37.64, 7.97) * mm, v(37.21, 7.63) * mm, v(36.63, 7.51) * mm, v(37.03, 7.24) * mm, v(37.76, 6.38) * mm, v(38.03, 5.68) * mm, v(37.85, 5.2) * mm, v(36.7, 4.74) * mm, v(34.28, 4.74) * mm, v(33.1, 5.04) * mm, v(32.8, 5.35) * mm, v(32.33, 5.1) * mm, v(31.33, 4.83) * mm, v(29.38, 4.64) * mm, v(27.94, 4.95) * mm, v(27.43, 5.4) * mm, v(27.46, 6.08) * mm, v(28.07, 7.02) * mm, v(28.92, 7.48) * mm]});
            skFitSpline(sketch, "E170", {"points": [v(31.57, 9.89) * mm, v(31.36, 10.16) * mm, v(31.27, 10.99) * mm, v(31.36, 12) * mm, v(31.63, 12.33) * mm, v(31.94, 12.27) * mm, v(32.24, 11.69) * mm, v(32.24, 10.68) * mm, v(32, 9.92) * mm, v(31.57, 9.89) * mm]});
            skFitSpline(sketch, "E171", {"points": [v(33.07, 11.2) * mm, v(33.19, 11.84) * mm, v(33.34, 12.2) * mm, v(33.55, 12.36) * mm, v(33.83, 12.27) * mm, v(34.07, 11.63) * mm, v(34.1, 10.77) * mm, v(33.95, 10.1) * mm, v(33.64, 9.8) * mm, v(33.25, 10.16) * mm, v(33.1, 10.71) * mm, v(33.07, 11.2) * mm]});
            skFitSpline(sketch, "E172", {"points": [v(32.23, 9.77) * mm, v(32.27, 9.4) * mm, v(32.4, 9.04) * mm, v(32.69, 8.94) * mm, v(32.95, 9.02) * mm, v(33.16, 9.46) * mm, v(33.14, 9.73) * mm, v(32.95, 9.88) * mm, v(32.43, 9.88) * mm, v(32.23, 9.77) * mm]});
            skFitSpline(sketch, "E173", {"points": [v(31.75, 11.2) * mm, v(31.53, 11.35) * mm, v(31.45, 11.8) * mm, v(31.6, 12.12) * mm, v(31.78, 12.15) * mm, v(31.94, 12.04) * mm, v(32.04, 11.56) * mm, v(31.94, 11.32) * mm, v(31.75, 11.2) * mm]});
            skFitSpline(sketch, "E174", {"points": [v(33.63, 11.22) * mm, v(33.46, 11.28) * mm, v(33.34, 11.6) * mm, v(33.46, 12.06) * mm, v(33.64, 12.1) * mm, v(33.82, 12) * mm, v(33.87, 11.58) * mm, v(33.76, 11.3) * mm, v(33.63, 11.22) * mm]});
            skFitSpline(sketch, "E175", {"points": [v(32.69, 9.54) * mm, v(32.9, 9.47) * mm, v(32.99, 9.39) * mm, v(32.9, 9.21) * mm, v(32.69, 9.16) * mm, v(32.49, 9.21) * mm, v(32.4, 9.4) * mm, v(32.53, 9.5) * mm, v(32.69, 9.54) * mm]});
            skFitSpline(sketch, "E176", {"points": [v(32.69, 5.64) * mm, v(33.34, 5.66) * mm, v(34.32, 5.94) * mm, v(35.2, 6.46) * mm, v(36, 7.34) * mm, v(36.23, 7.66) * mm, v(36.02, 7.78) * mm, v(36.02, 7.96) * mm, v(36.33, 7.82) * mm, v(36.8, 7.79) * mm, v(37.18, 7.97) * mm, v(37.48, 8.33) * mm, v(37.52, 8.82) * mm, v(37.48, 9.33) * mm, v(37.06, 10.2) * mm, v(36.75, 10.5) * mm, v(36.63, 10.82) * mm, v(36.33, 11.58) * mm, v(35.94, 12.27) * mm, v(35.02, 13.12) * mm, v(34.07, 13.62) * mm, v(32.69, 13.86) * mm, v(31.36, 13.62) * mm, v(30.4, 13.12) * mm, v(30.02, 12.76) * mm, v(29.63, 12.57) * mm, v(29.67, 12.76) * mm, v(29.4, 13.12) * mm, v(28.76, 13.44) * mm, v(28.1, 13.27) * mm, v(27.73, 12.61) * mm, v(27.65, 12.04) * mm, v(27.85, 11.08) * mm, v(28.37, 10.35) * mm, v(28.6, 10.49) * mm, v(28.6, 10.16) * mm, v(28.6, 9.21) * mm, v(28.72, 8.54) * mm, v(29.22, 7.51) * mm, v(30.21, 6.44) * mm, v(31.45, 5.8) * mm, v(32.69, 5.64) * mm]});
            skFitSpline(sketch, "E177", {"points": [v(32.13, 5.44) * mm, v(31.33, 5.57) * mm, v(29.67, 6.58) * mm, v(29.06, 7.28) * mm, v(28.26, 6.75) * mm, v(27.8, 6.13) * mm, v(27.67, 5.66) * mm, v(28, 5.26) * mm, v(29.04, 5.04) * mm, v(30.78, 5.07) * mm, v(31.85, 5.22) * mm, v(32.13, 5.44) * mm]});
            skFitSpline(sketch, "E178", {"points": [v(33.23, 5.41) * mm, v(33.65, 5.24) * mm, v(35, 5) * mm, v(36.84, 5.07) * mm, v(37.63, 5.41) * mm, v(37.65, 5.9) * mm, v(37.22, 6.64) * mm, v(36.31, 7.28) * mm, v(36.12, 7.06) * mm, v(35.16, 6.17) * mm, v(34.52, 5.77) * mm, v(33.23, 5.41) * mm]});
            skCircle(sketch, "E179.0", {"center": v(45.98, 9) * mm, "radius": 2.87 * mm});
            skCircle(sketch, "E180.0", {"center": v(58.02, 9) * mm, "radius": 2.87 * mm});
            skLineSegment(sketch, "E181", {"start": v(58.02, 9) * mm, "end": v(58.02, 22.43) * mm});
            skFitSpline(sketch, "E182.MirrorC", {"points": [v(83.35, 9.54) * mm, v(83.13, 9.47) * mm, v(83.05, 9.39) * mm, v(83.15, 9.21) * mm, v(83.35, 9.16) * mm, v(83.55, 9.21) * mm, v(83.64, 9.4) * mm, v(83.51, 9.5) * mm, v(83.35, 9.54) * mm]});
            skFitSpline(sketch, "E183.MirrorC", {"points": [v(82.41, 11.22) * mm, v(82.58, 11.28) * mm, v(82.7, 11.6) * mm, v(82.58, 12.06) * mm, v(82.4, 12.1) * mm, v(82.22, 12) * mm, v(82.17, 11.58) * mm, v(82.28, 11.3) * mm, v(82.41, 11.22) * mm]});
            skFitSpline(sketch, "E184.MirrorC", {"points": [v(84.29, 11.2) * mm, v(84.5, 11.35) * mm, v(84.59, 11.8) * mm, v(84.44, 12.12) * mm, v(84.26, 12.15) * mm, v(84.1, 12.04) * mm, v(84, 11.56) * mm, v(84.1, 11.32) * mm, v(84.29, 11.2) * mm]});
            skFitSpline(sketch, "E185.MirrorC", {"points": [v(83.81, 9.77) * mm, v(83.77, 9.4) * mm, v(83.64, 9.04) * mm, v(83.35, 8.94) * mm, v(83.1, 9.02) * mm, v(82.88, 9.46) * mm, v(82.9, 9.73) * mm, v(83.1, 9.88) * mm, v(83.6, 9.88) * mm, v(83.81, 9.77) * mm]});
            skFitSpline(sketch, "E186.MirrorC", {"points": [v(82.97, 11.2) * mm, v(82.85, 11.84) * mm, v(82.7, 12.2) * mm, v(82.49, 12.36) * mm, v(82.21, 12.27) * mm, v(81.97, 11.63) * mm, v(81.94, 10.77) * mm, v(82.1, 10.1) * mm, v(82.4, 9.8) * mm, v(82.8, 10.16) * mm, v(82.94, 10.71) * mm, v(82.97, 11.2) * mm]});
            skFitSpline(sketch, "E187.MirrorC", {"points": [v(84.47, 9.89) * mm, v(84.68, 10.16) * mm, v(84.77, 10.99) * mm, v(84.68, 12) * mm, v(84.4, 12.33) * mm, v(84.1, 12.27) * mm, v(83.8, 11.69) * mm, v(83.8, 10.68) * mm, v(84.04, 9.92) * mm, v(84.47, 9.89) * mm]});
            skFitSpline(sketch, "E188.MirrorC", {"points": [v(83.35, 5.64) * mm, v(82.7, 5.66) * mm, v(81.72, 5.94) * mm, v(80.84, 6.46) * mm, v(80.04, 7.34) * mm, v(79.8, 7.66) * mm, v(80.02, 7.78) * mm, v(80.02, 7.96) * mm, v(79.7, 7.82) * mm, v(79.25, 7.79) * mm, v(78.86, 7.97) * mm, v(78.56, 8.33) * mm, v(78.52, 8.82) * mm, v(78.56, 9.33) * mm, v(78.98, 10.2) * mm, v(79.3, 10.5) * mm, v(79.4, 10.82) * mm, v(79.7, 11.58) * mm, v(80.1, 12.27) * mm, v(81.02, 13.12) * mm, v(81.97, 13.62) * mm, v(83.35, 13.86) * mm, v(84.68, 13.62) * mm, v(85.64, 13.12) * mm, v(86.02, 12.76) * mm, v(86.41, 12.57) * mm, v(86.37, 12.76) * mm, v(86.64, 13.12) * mm, v(87.28, 13.44) * mm, v(87.94, 13.27) * mm, v(88.3, 12.61) * mm, v(88.39, 12.04) * mm, v(88.19, 11.08) * mm, v(87.67, 10.35) * mm, v(87.44, 10.49) * mm, v(87.44, 10.16) * mm, v(87.44, 9.21) * mm, v(87.32, 8.54) * mm, v(86.82, 7.51) * mm, v(85.83, 6.44) * mm, v(84.59, 5.8) * mm, v(83.35, 5.64) * mm]});
            skFitSpline(sketch, "E189.MirrorC", {"points": [v(83.9, 5.44) * mm, v(84.71, 5.57) * mm, v(86.37, 6.58) * mm, v(86.98, 7.28) * mm, v(87.78, 6.75) * mm, v(88.24, 6.13) * mm, v(88.37, 5.66) * mm, v(88.04, 5.26) * mm, v(87, 5.04) * mm, v(85.26, 5.07) * mm, v(84.19, 5.22) * mm, v(83.9, 5.44) * mm]});
            skFitSpline(sketch, "E190.MirrorC", {"points": [v(82.8, 5.41) * mm, v(82.4, 5.24) * mm, v(81.03, 5) * mm, v(79.2, 5.07) * mm, v(78.4, 5.41) * mm, v(78.39, 5.9) * mm, v(78.82, 6.64) * mm, v(79.73, 7.28) * mm, v(79.92, 7.06) * mm, v(80.88, 6.17) * mm, v(81.52, 5.77) * mm, v(82.8, 5.41) * mm]});
            skFitSpline(sketch, "E191.MirrorC", {"points": [v(87.12, 7.48) * mm, v(87.49, 8.18) * mm, v(87.73, 9.22) * mm, v(87.67, 9.98) * mm, v(87.94, 10.2) * mm, v(88.5, 11.17) * mm, v(88.68, 12.36) * mm, v(88.31, 13.33) * mm, v(87.27, 13.73) * mm, v(86.36, 13.27) * mm, v(86.18, 13.12) * mm, v(86.02, 13.27) * mm, v(84.4, 14.03) * mm, v(82.06, 14) * mm, v(80.41, 13.09) * mm, v(79.26, 11.41) * mm, v(79.07, 10.68) * mm, v(78.77, 10.44) * mm, v(78.3, 9.61) * mm, v(78.22, 8.64) * mm, v(78.4, 7.97) * mm, v(78.83, 7.63) * mm, v(79.4, 7.51) * mm, v(79.01, 7.24) * mm, v(78.28, 6.38) * mm, v(78, 5.68) * mm, v(78.19, 5.2) * mm, v(79.35, 4.74) * mm, v(81.76, 4.74) * mm, v(82.94, 5.04) * mm, v(83.25, 5.35) * mm, v(83.7, 5.1) * mm, v(84.71, 4.83) * mm, v(86.66, 4.64) * mm, v(88.1, 4.95) * mm, v(88.62, 5.4) * mm, v(88.58, 6.08) * mm, v(87.97, 7.02) * mm, v(87.12, 7.48) * mm]});
            skLineSegment(sketch, "E192", {"start": v(84.71, 5.57) * mm, "end": v(84.59, 5.8) * mm});
            skSolve(sketch);
        }
        {
            var Q0;
            Q0=makeQuery(id+"F17.imprint","IMPRINT",FACE,{"disambiguationData":[TD([[makeQuery(id+"F17.imprint","IMPRINT",EDGE,{"derivedFrom":sQuery(id+"F17.wireOp",EDGE,"E188.MirrorC")}),1.0]])]});
            var Q1;
            Q1=makeQuery(id+"F17.imprint","IMPRINT",FACE,{"disambiguationData":[TD([[makeQuery(id+"F17.imprint","IMPRINT",EDGE,{"derivedFrom":sQuery(id+"F17.wireOp",EDGE,"E184.MirrorC")}),-1.0]])]});
            var Q2;
            Q2=makeQuery(id+"F17.imprint","IMPRINT",FACE,{"disambiguationData":[TD([[makeQuery(id+"F17.imprint","IMPRINT",EDGE,{"derivedFrom":sQuery(id+"F17.wireOp",EDGE,"E183.MirrorC")}),-1.0]])]});
            var Q3;
            Q3=makeQuery(id+"F17.imprint","IMPRINT",FACE,{"disambiguationData":[TD([[makeQuery(id+"F17.imprint","IMPRINT",EDGE,{"derivedFrom":sQuery(id+"F17.wireOp",EDGE,"E182.MirrorC")}),-1.0]])]});
            var Q4;
            Q4=makeQuery(id+"F17.imprint","IMPRINT",FACE,{"disambiguationData":[TD([[makeQuery(id+"F17.imprint","IMPRINT",EDGE,{"derivedFrom":sQuery(id+"F17.wireOp",EDGE,"E169")}),-1.0]])]});
            var Q5;
            Q5=makeQuery(id+"F17.imprint","IMPRINT",FACE,{"disambiguationData":[TD([[makeQuery(id+"F17.imprint","IMPRINT",EDGE,{"derivedFrom":sQuery(id+"F17.wireOp",EDGE,"E171")}),-1.0]])]});
            var Q6;
            Q6=makeQuery(id+"F17.imprint","IMPRINT",FACE,{"disambiguationData":[TD([[makeQuery(id+"F17.imprint","IMPRINT",EDGE,{"derivedFrom":sQuery(id+"F17.wireOp",EDGE,"E172")}),1.0]])]});
            var Q7;
            Q7=makeQuery(id+"F17.imprint","IMPRINT",FACE,{"disambiguationData":[TD([[makeQuery(id+"F17.imprint","IMPRINT",EDGE,{"derivedFrom":sQuery(id+"F17.wireOp",EDGE,"E170")}),-1.0]])]});
            var Q8;
            Q8=sQuery(id+"F17.wireOp",EDGE,"E191.MirrorC");
            extrude(context, id + "F18", {"entities" : qUnion([Q0, Q1, Q2, Q3, Q4, Q5, Q6, Q7]), "operationType" : NewBodyOperationType.REMOVE, "surfaceEntities" : qUnion([Q8]), "oppositeDirection" : true, "depth" : .5 * mm, "offsetDistance" : 25 * mm});
        }
    });
